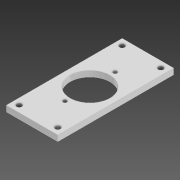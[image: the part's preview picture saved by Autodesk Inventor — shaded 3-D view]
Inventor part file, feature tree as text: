
AUTODESK INVENTOR PART (.ipt)
format: ipt  version: 2020 (Build 240168000, 168)  size: 110,080 bytes
history: native  units: in
note: dims shown in document units (in); Inventor stores cm internally (conversion verified against a paired STEP export)
features: extrude x1, sketch x1
ambient origin geometry x8: Origin, YZ Plane, XZ Plane, XY Plane, X Axis, Y Axis, Z Axis, Center Point
bodies: Solid1 (feature_tree)
feature tree (2):
  extrude  "Extrusion1"  Depth=3.5433in
  sketch  "Sketch1"  dims[d0=1.5748in d1=3.5433in d2=1.2205in d3=0.7677in d4=1.5354in d5=0.1181in d6=0.1181in d7=0.1772in d8=0.0in d9=1.1811in d10=3.1496in d11=0.1575in d12=0.1575in d13=0.1575in d14=0.1575in]
